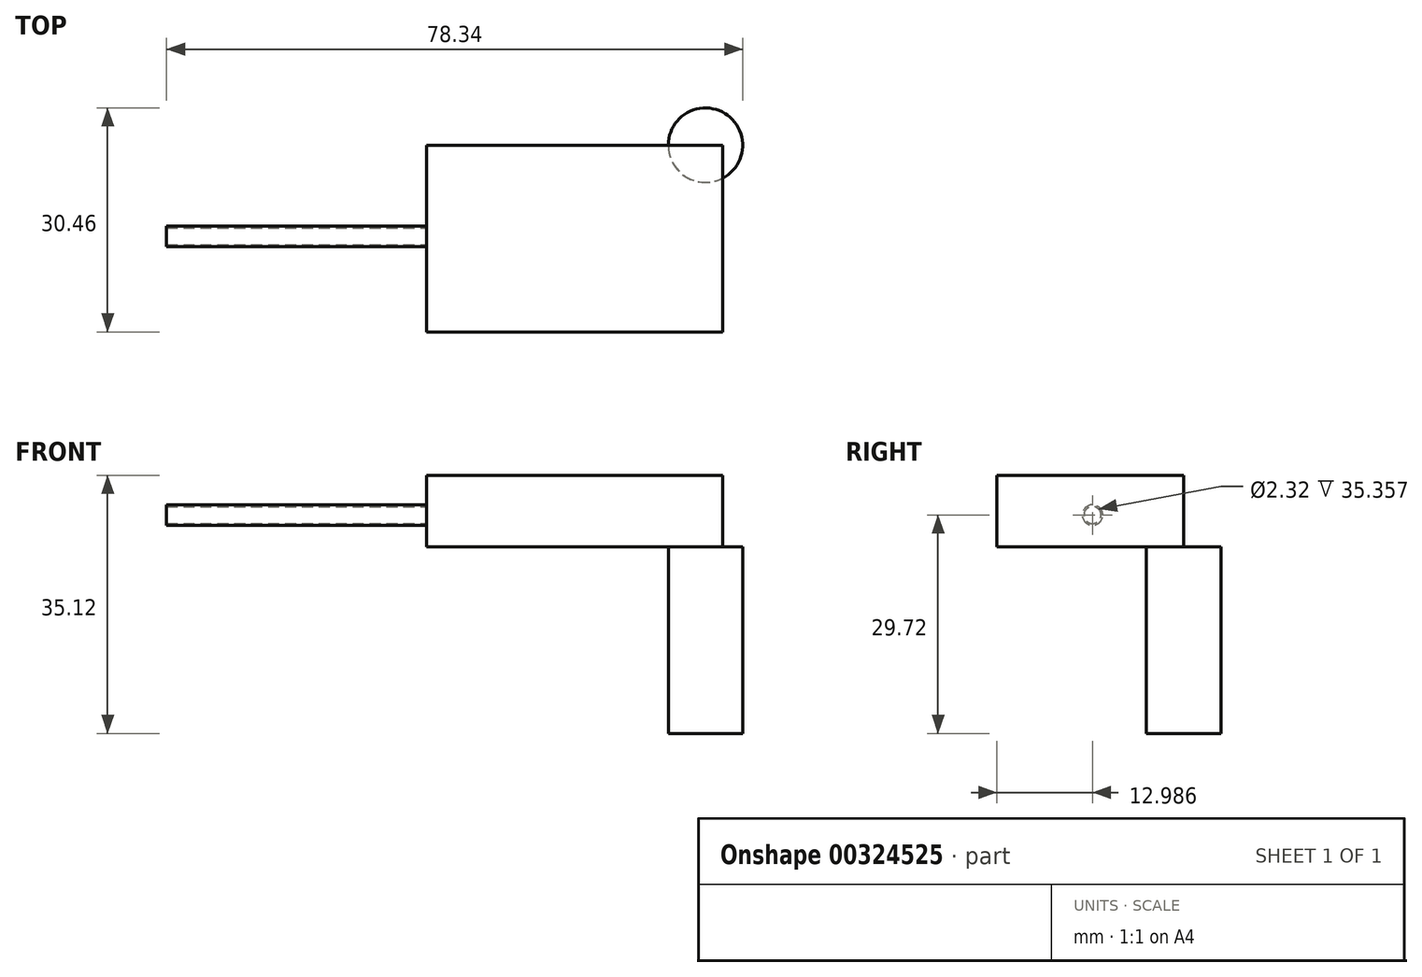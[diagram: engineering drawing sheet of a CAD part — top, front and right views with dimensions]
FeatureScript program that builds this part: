
annotation { "Feature Type Name" : "Feature", "Feature Type Description" : "" }
export const myFeature = defineFeature(function(context is Context, id is Id, definition is map)
    precondition{}
    {
        {
            var Q0;
            Q0=qCreatedBy(makeId("Front.planeOp"),FACE);
            var sketch = newSketch(context, id + "F0", { "sketchPlane" : qUnion([Q0])});
            skLineSegment(sketch, "E0.bottom", {"start": v(-84.15, 54.02) * mm, "end": v(-124.38, 54.02) * mm});
            skLineSegment(sketch, "E0.top", {"start": v(-84.15, 44.3) * mm, "end": v(-124.38, 44.3) * mm});
            skLineSegment(sketch, "E0.left", {"start": v(-84.15, 54.02) * mm, "end": v(-84.15, 44.3) * mm});
            skLineSegment(sketch, "E0.right", {"start": v(-124.38, 54.02) * mm, "end": v(-124.38, 44.3) * mm});
            skSolve(sketch);
        }
        {
            var Q0;
            Q0 = qSketchRegion(id + "F0", true);
            extrude(context, id + "F1", {"entities" : qUnion([Q0]), "depth" : 25.4 * mm});
        }
        {
            var Q0;
            Q0=makeQuery(id+"F1.opExtrude","SWEPT_FACE",FACE,{"disambiguationData":[OSD([sQuery(id+"F0.wireOp",EDGE,"E0.right")])]});
            var sketch = newSketch(context, id + "F2", { "sketchPlane" : qUnion([Q0])});
            skCircle(sketch, "E1", {"center": v(12.41, 48.62) * mm, "radius": 1.16 * mm});
            skCircle(sketch, "E2", {"center": v(12.41, 48.62) * mm, "radius": 1.39 * mm});
            skSolve(sketch);
        }
        {
            var Q0;
            Q0 = qSketchRegion(id + "F2", true);
            extrude(context, id + "F3", {"entities" : qUnion([Q0]), "operationType" : NewBodyOperationType.ADD, "depth" : 35.36 * mm});
        }
        {
            var Q0;
            Q0=makeQuery(id+"F1.opExtrude","SWEPT_FACE",FACE,{"disambiguationData":[OSD([sQuery(id+"F0.wireOp",EDGE,"E0.top")])]});
            var sketch = newSketch(context, id + "F4", { "sketchPlane" : qUnion([Q0])});
            skCircle(sketch, "E3", {"center": v(-86.47, 0) * mm, "radius": 5.06 * mm});
            skSolve(sketch);
        }
        {
            var Q0;
            Q0 = qSketchRegion(id + "F4", true);
            extrude(context, id + "F5", {"entities" : qUnion([Q0]), "operationType" : NewBodyOperationType.ADD, "depth" : 25.4 * mm});
        }
    });
